# Revit family: STR4P
name_source: partatom
category: Plumbing Fixtures
revit_build: Autodesk Revit 2015 (Build: 20140322_1515(x64)
units: mm (PartAtom-declared; Revit-internal decimal feet)

## types (9) — shared parameters
Glass = Glass
H = 2000 mm  [stored 6.56168 ft]
L1 = 900 mm  [stored 2.95276 ft]
Manufacturer = SanSwiss
Metal = Aluminum - Polished
Model = STR4P
Type Comments = WALK-IN-EASY
URL = www.sanswiss.com
zero-valued in all types: Number of elements, Width fixed panel, Width fixed panel 2

## per-type parameters (varying)
| type | L2 |
| 800 | 800 mm  [stored 2.62467 ft] |
| 900 | 900 mm  [stored 2.95276 ft] |
| 1000 | 1000 mm  [stored 3.28084 ft] |
| 1100 | 1100 mm |
| 1200 | 1200 mm |
| 1300 | 1300 mm |
| 1400 | 1400 mm |
| 1500 | 1500 mm |
| 1600 | 1600 mm  [stored 5.24934 ft] |

note: [stored X ft] marks values corroborated as IEEE doubles in the binary element streams (Revit-internal decimal feet)

## geometry (parser evidence)
native form markers: Sweep x7
no freeform markers — native parametric forms only
